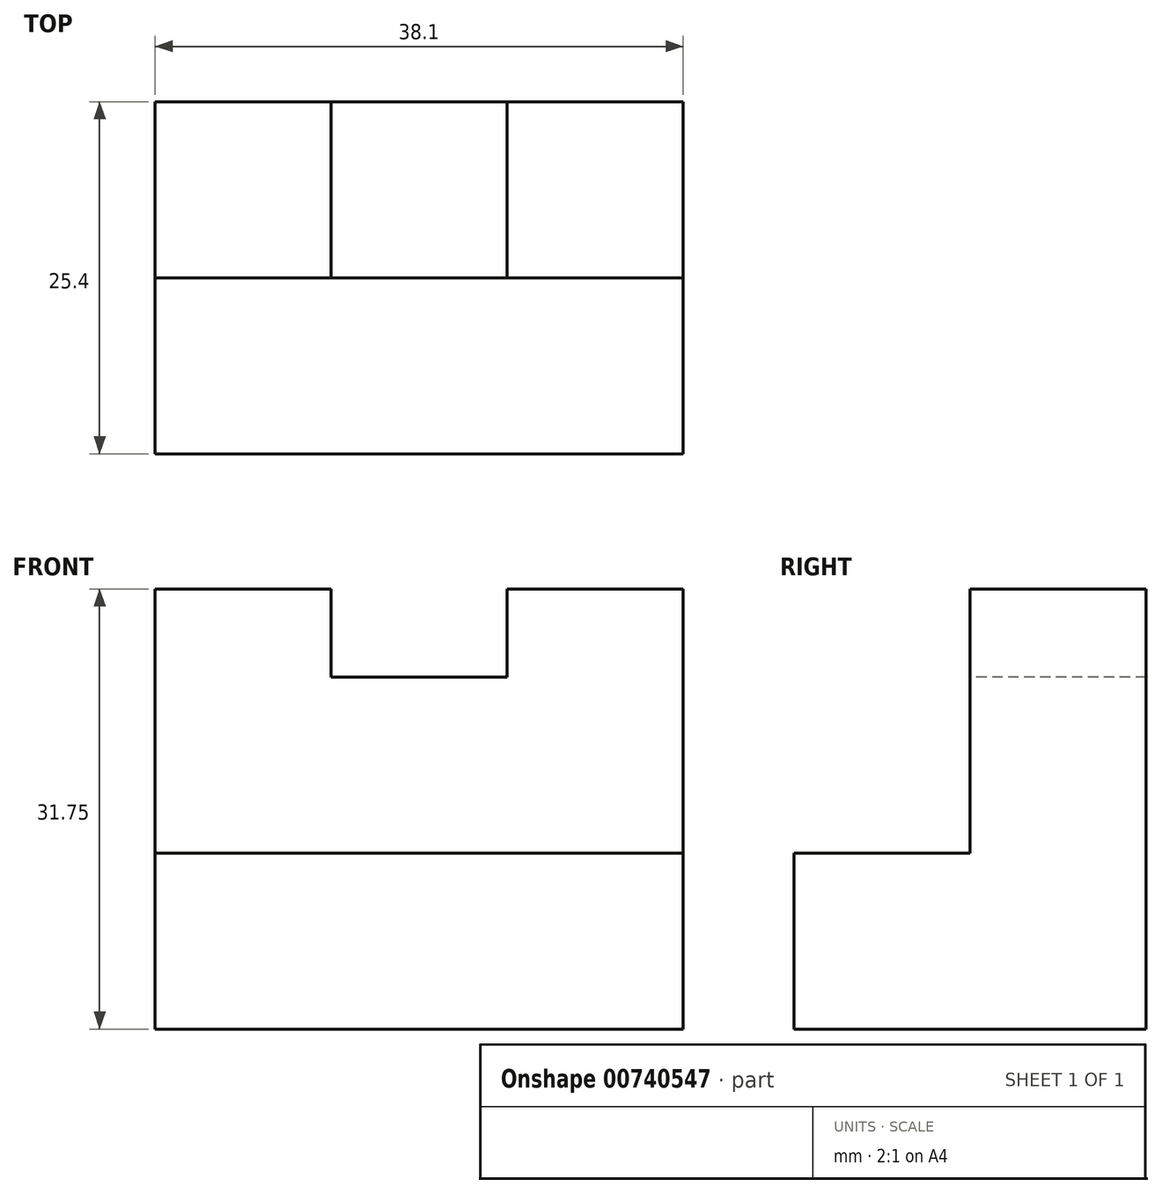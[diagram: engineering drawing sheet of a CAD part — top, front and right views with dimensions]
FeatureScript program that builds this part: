
annotation { "Feature Type Name" : "Feature", "Feature Type Description" : "" }
export const myFeature = defineFeature(function(context is Context, id is Id, definition is map)
    precondition{}
    {
        {
            var Q0;
            Q0=qCreatedBy(makeId("Right.planeOp"),FACE);
            var sketch = newSketch(context, id + "F0", { "sketchPlane" : qUnion([Q0])});
            skLineSegment(sketch, "E0", {"start": v(0, 0) * mm, "end": v(0, 31.75) * mm});
            skLineSegment(sketch, "E1", {"start": v(0, 31.75) * mm, "end": v(-12.7, 31.75) * mm});
            skLineSegment(sketch, "E2", {"start": v(-12.7, 31.75) * mm, "end": v(-12.7, 12.7) * mm});
            skLineSegment(sketch, "E3", {"start": v(-12.7, 12.7) * mm, "end": v(-25.4, 12.7) * mm});
            skLineSegment(sketch, "E4", {"start": v(-25.4, 12.7) * mm, "end": v(-25.4, 0) * mm});
            skLineSegment(sketch, "E5", {"start": v(-25.4, 0) * mm, "end": v(0, 0) * mm});
            skSolve(sketch);
        }
        {
            var Q0;
            Q0 = qSketchRegion(id + "F0", true);
            extrude(context, id + "F1", {"entities" : qUnion([Q0]), "depth" : 38.1 * mm, "offsetDistance" : 25.4 * mm});
        }
        {
            var Q0;
            Q0=makeQuery(id+"F1.opExtrude","SWEPT_FACE",FACE,{"disambiguationData":[OSD([sQuery(id+"F0.wireOp",EDGE,"E2")])]});
            var sketch = newSketch(context, id + "F2", { "sketchPlane" : qUnion([Q0])});
            skLineSegment(sketch, "E6", {"start": v(25.4, 31.75) * mm, "end": v(25.4, 25.4) * mm});
            skLineSegment(sketch, "E7", {"start": v(25.4, 25.4) * mm, "end": v(12.7, 25.4) * mm});
            skLineSegment(sketch, "E8", {"start": v(12.7, 31.75) * mm, "end": v(12.7, 25.4) * mm});
            skLineSegment(sketch, "E9", {"start": v(25.4, 31.75) * mm, "end": v(38.1, 31.75) * mm});
            skSolve(sketch);
        }
        {
            var Q0;
            Q0 = qSketchRegion(id + "F2", true);
            var Q1;
            {var subQ0=sQuery(id+"F2.wireOp",EDGE,"E6");Q1=makeQuery(id+"F2.imprint","IMPRINT",FACE,{"disambiguationData":[TD([[makeQuery(id+"F2.imprint","IMPRINT",EDGE,{"derivedFrom":subQ0}),-1.0]])]});}
            extrude(context, id + "F3", {"entities" : qUnion([Q0, Q1]), "operationType" : NewBodyOperationType.REMOVE, "endBound" : BoundingType.THROUGH_ALL, "oppositeDirection" : true, "depth" : 25.4 * mm, "offsetDistance" : 25.4 * mm});
        }
    });
